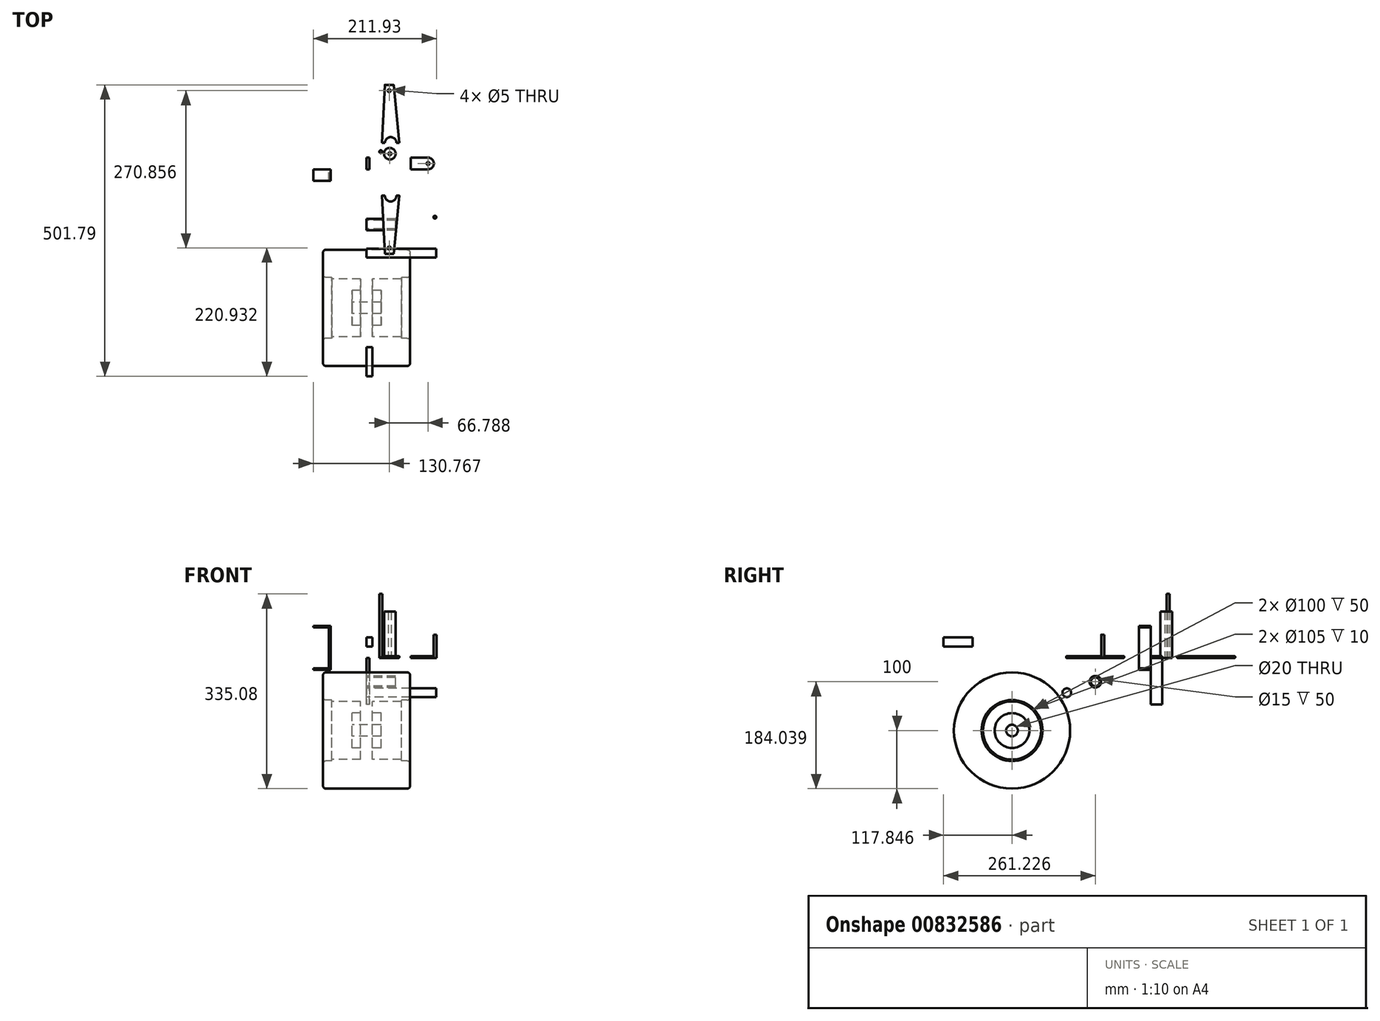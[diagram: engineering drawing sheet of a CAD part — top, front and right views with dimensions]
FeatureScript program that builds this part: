
annotation { "Feature Type Name" : "Feature", "Feature Type Description" : "" }
export const myFeature = defineFeature(function(context is Context, id is Id, definition is map)
    precondition{}
    {
        {
            var Q0;
            Q0=qCreatedBy(makeId("Top.planeOp"),FACE);
            var sketch = newSketch(context, id + "F0", { "sketchPlane" : qUnion([Q0])});
            skLineSegment(sketch, "E0", {"start": v(75.84, 20) * mm, "end": v(75.84, 0) * mm});
            skLineSegment(sketch, "E1", {"start": v(75.84, 0) * mm, "end": v(105.84, 0) * mm});
            skLineSegment(sketch, "E2", {"start": v(105.84, 20) * mm, "end": v(75.84, 20) * mm});
            skArc(sketch, "E3", {"start": v(105.84, 0) * mm, "mid": v(115.84, 10) * mm, "end": v(105.84, 20) * mm});
            skCircle(sketch, "E4", {"center": v(105.84, 10) * mm, "radius": 2.5 * mm});
            skSolve(sketch);
        }
        {
            var Q0;
            Q0=qCreatedBy(makeId("Right.planeOp"),FACE);
            var sketch = newSketch(context, id + "F1", { "sketchPlane" : qUnion([Q0])});
            skLineSegment(sketch, "E5", {"start": v(0, 0) * mm, "end": v(0, -80) * mm});
            skLineSegment(sketch, "E6", {"start": v(0, -80) * mm, "end": v(20, -80) * mm});
            skLineSegment(sketch, "E7", {"start": v(20, -80) * mm, "end": v(20, 0) * mm});
            skLineSegment(sketch, "E8", {"start": v(20, 0) * mm, "end": v(0, 0) * mm});
            skSolve(sketch);
        }
        {
            var Q0;
            Q0 = qSketchRegion(id + "F1", true);
            extrude(context, id + "F2", {"entities" : qUnion([Q0]), "depth" : 5 * mm, "offsetDistance" : 25.4 * mm});
        }
        {
            var Q0;
            Q0=qCreatedBy(makeId("Top.planeOp"),FACE);
            var sketch = newSketch(context, id + "F3", { "sketchPlane" : qUnion([Q0])});
            skCircle(sketch, "E9", {"center": v(24.54, 30.27) * mm, "radius": 2.5 * mm});
            skSolve(sketch);
        }
        {
            var Q0;
            Q0=qCreatedBy(makeId("Top.planeOp"),FACE);
            var sketch = newSketch(context, id + "F4", { "sketchPlane" : qUnion([Q0])});
            skCircle(sketch, "E10", {"center": v(40.1, 26.85) * mm, "radius": 10 * mm});
            skCircle(sketch, "E11", {"center": v(40.1, 26.85) * mm, "radius": 2.5 * mm});
            skSolve(sketch);
        }
        {
            var Q0;
            Q0=makeQuery(id+"F3.imprint","IMPRINT",FACE,{"disambiguationData":[TD([[makeQuery(id+"F3.imprint","IMPRINT",EDGE,{"derivedFrom":sQuery(id+"F3.wireOp",EDGE,"E9")}),1.0]])]});
            extrude(context, id + "F5", {"entities" : qUnion([Q0]), "depth" : 110 * mm, "offsetDistance" : 25.4 * mm});
        }
        {
            var Q0;
            Q0=makeQuery(id+"F4.imprint","IMPRINT",FACE,{"disambiguationData":[TD([[makeQuery(id+"F4.imprint","IMPRINT",EDGE,{"derivedFrom":sQuery(id+"F4.wireOp",EDGE,"E10")}),1.0]])]});
            extrude(context, id + "F6", {"entities" : qUnion([Q0]), "depth" : 80 * mm, "offsetDistance" : 25.4 * mm});
        }
        {
            var Q0;
            Q0=qCreatedBy(makeId("Top.planeOp"),FACE);
            var sketch = newSketch(context, id + "F7", { "sketchPlane" : qUnion([Q0])});
            skArc(sketch, "E12", {"start": v(31.55, -45.43) * mm, "mid": v(41.55, -55.43) * mm, "end": v(51.55, -45.43) * mm});
            skLineSegment(sketch, "E13", {"start": v(31.55, -145.43) * mm, "end": v(26.55, -45.43) * mm});
            skLineSegment(sketch, "E14", {"start": v(51.55, -45.43) * mm, "end": v(56.55, -45.43) * mm});
            skLineSegment(sketch, "E15", {"start": v(56.55, -45.43) * mm, "end": v(46.55, -145.43) * mm});
            skLineSegment(sketch, "E16", {"start": v(26.55, -45.43) * mm, "end": v(31.55, -45.43) * mm});
            skLineSegment(sketch, "E17", {"start": v(31.55, -145.43) * mm, "end": v(46.55, -145.43) * mm});
            skCircle(sketch, "E18", {"center": v(39.05, -135.43) * mm, "radius": 2.5 * mm});
            skSolve(sketch);
        }
        {
            var Q0;
            Q0=makeQuery(id+"F7.imprint","IMPRINT",FACE,{"disambiguationData":[TD([[makeQuery(id+"F7.imprint","IMPRINT",EDGE,{"derivedFrom":sQuery(id+"F7.wireOp",EDGE,"E12")}),-1.0]])]});
            extrude(context, id + "F8", {"entities" : qUnion([Q0]), "depth" : 3 * mm, "offsetDistance" : 25.4 * mm});
        }
        {
            var Q0;
            Q0=qCreatedBy(makeId("Top.planeOp"),FACE);
            var sketch = newSketch(context, id + "F9", { "sketchPlane" : qUnion([Q0])});
            skCircle(sketch, "E19", {"center": v(117.71, -82.43) * mm, "radius": 2.5 * mm});
            skSolve(sketch);
        }
        {
            var Q0;
            Q0=makeQuery(id+"F9.imprint","IMPRINT",FACE,{"disambiguationData":[TD([[makeQuery(id+"F9.imprint","IMPRINT",EDGE,{"derivedFrom":sQuery(id+"F9.wireOp",EDGE,"E19")}),1.0]])]});
            extrude(context, id + "F10", {"entities" : qUnion([Q0]), "depth" : 40 * mm, "offsetDistance" : 25.4 * mm});
        }
        {
            var Q0;
            Q0=makeQuery(id+"F0.imprint","IMPRINT",FACE,{"disambiguationData":[TD([[makeQuery(id+"F0.imprint","IMPRINT",EDGE,{"derivedFrom":sQuery(id+"F0.wireOp",EDGE,"E0")}),1.0]])]});
            extrude(context, id + "F11", {"entities" : qUnion([Q0]), "depth" : 3 * mm, "offsetDistance" : 25 * mm});
        }
        {
            var Q0;
            Q0=qCreatedBy(makeId("Front.planeOp"),FACE);
            var sketch = newSketch(context, id + "F12", { "sketchPlane" : qUnion([Q0])});
            skLineSegment(sketch, "E20.bottom", {"start": v(-91.72, -20.78) * mm, "end": v(-61.72, -20.78) * mm});
            skLineSegment(sketch, "E20.top", {"start": v(-91.72, -17.78) * mm, "end": v(-61.72, -17.78) * mm});
            skLineSegment(sketch, "E20.left", {"start": v(-91.72, -20.78) * mm, "end": v(-91.72, -17.78) * mm});
            skLineSegment(sketch, "E20.right", {"start": v(-61.72, -20.78) * mm, "end": v(-61.72, -17.78) * mm});
            skLineSegment(sketch, "E21.bottom", {"start": v(-61.72, 52.22) * mm, "end": v(-91.72, 52.22) * mm});
            skLineSegment(sketch, "E21.top", {"start": v(-61.72, 55.22) * mm, "end": v(-91.72, 55.22) * mm});
            skLineSegment(sketch, "E21.left", {"start": v(-61.72, 52.22) * mm, "end": v(-61.72, 55.22) * mm});
            skLineSegment(sketch, "E21.right", {"start": v(-91.72, 52.22) * mm, "end": v(-91.72, 55.22) * mm});
            skLineSegment(sketch, "E22.bottom", {"start": v(-61.72, 52.22) * mm, "end": v(-64.72, 52.22) * mm});
            skLineSegment(sketch, "E22.top", {"start": v(-61.72, -17.78) * mm, "end": v(-64.72, -17.78) * mm});
            skLineSegment(sketch, "E22.left", {"start": v(-61.72, 52.22) * mm, "end": v(-61.72, -17.78) * mm});
            skLineSegment(sketch, "E22.right", {"start": v(-64.72, 52.22) * mm, "end": v(-64.72, -17.78) * mm});
            skSolve(sketch);
        }
        {
            var Q0;
            Q0=makeQuery(id+"F12.imprint","IMPRINT",FACE,{"disambiguationData":[TD([[makeQuery(id+"F12.imprint","IMPRINT",EDGE,{"derivedFrom":sQuery(id+"F12.wireOp",EDGE,"E21.top")}),1.0]])]});
            var Q1;
            Q1=makeQuery(id+"F12.imprint","IMPRINT",FACE,{"disambiguationData":[TD([[makeQuery(id+"F12.imprint","IMPRINT",EDGE,{"derivedFrom":sQuery(id+"F12.wireOp",EDGE,"E20.bottom")}),1.0]])]});
            extrude(context, id + "F13", {"entities" : qUnion([Q0, Q1]), "depth" : 20 * mm, "offsetDistance" : 25 * mm});
        }
        {
            var Q0;
            {var subQ0=sQuery(id+"F12.wireOp",EDGE,"E22.left");Q0=makeQuery(id+"F12.imprint","IMPRINT",FACE,{"disambiguationData":[TD([[makeQuery(id+"F12.imprint","IMPRINT",EDGE,{"derivedFrom":subQ0}),-1.0]])]});}
            extrude(context, id + "F14", {"entities" : qUnion([Q0]), "depth" : 20 * mm, "offsetDistance" : 25 * mm});
        }
        {
            var Q0;
            Q0=qCreatedBy(makeId("Right.planeOp"),FACE);
            var sketch = newSketch(context, id + "F15", { "sketchPlane" : qUnion([Q0])});
            skCircle(sketch, "E23", {"center": v(-95.13, -41.04) * mm, "radius": 10 * mm});
            skCircle(sketch, "E24", {"center": v(-95.13, -41.04) * mm, "radius": 7.5 * mm});
            skSolve(sketch);
        }
        {
            var Q0;
            Q0=makeQuery(id+"F15.imprint","IMPRINT",FACE,{"disambiguationData":[TD([[makeQuery(id+"F15.imprint","IMPRINT",EDGE,{"derivedFrom":sQuery(id+"F15.wireOp",EDGE,"E23")}),1.0]])]});
            extrude(context, id + "F16", {"entities" : qUnion([Q0]), "depth" : 50 * mm, "offsetDistance" : 25 * mm});
        }
        {
            var Q0;
            Q0=qCreatedBy(makeId("Right.planeOp"),FACE);
            var sketch = newSketch(context, id + "F17", { "sketchPlane" : qUnion([Q0])});
            skCircle(sketch, "E25", {"center": v(-144.24, -59.98) * mm, "radius": 7.5 * mm});
            skSolve(sketch);
        }
        {
            var Q0;
            Q0=qCreatedBy(makeId("Right.planeOp"),FACE);
            var sketch = newSketch(context, id + "F18", { "sketchPlane" : qUnion([Q0])});
            skCircle(sketch, "E26", {"center": v(-238.51, -125.08) * mm, "radius": 100 * mm});
            skCircle(sketch, "E27", {"center": v(-238.51, -125.08) * mm, "radius": 10 * mm});
            skCircle(sketch, "E28", {"center": v(-238.51, -125.08) * mm, "radius": 50 * mm});
            skCircle(sketch, "E29", {"center": v(-238.51, -125.08) * mm, "radius": 30 * mm});
            skCircle(sketch, "E30", {"center": v(-238.51, -125.08) * mm, "radius": 52.5 * mm});
            skSolve(sketch);
        }
        {
            var Q0;
            Q0=makeQuery(id+"F17.imprint","IMPRINT",FACE,{"disambiguationData":[TD([[makeQuery(id+"F17.imprint","IMPRINT",EDGE,{"derivedFrom":sQuery(id+"F17.wireOp",EDGE,"E25")}),1.0]])]});
            extrude(context, id + "F19", {"entities" : qUnion([Q0]), "depth" : 120 * mm, "offsetDistance" : 25 * mm});
        }
        {
            var Q0;
            Q0=makeQuery(id+"F18.imprint","IMPRINT",FACE,{"disambiguationData":[TD([[makeQuery(id+"F18.imprint","IMPRINT",EDGE,{"derivedFrom":sQuery(id+"F18.wireOp",EDGE,"E27")}),-1.0]])]});
            extrude(context, id + "F20", {"entities" : qUnion([Q0]), "endBound" : BoundingType.SYMMETRIC, "depth" : 50 * mm, "offsetDistance" : 25 * mm});
        }
        {
            var Q0;
            Q0=makeQuery(id+"F18.imprint","IMPRINT",FACE,{"disambiguationData":[TD([[makeQuery(id+"F18.imprint","IMPRINT",EDGE,{"derivedFrom":sQuery(id+"F18.wireOp",EDGE,"E28")}),1.0]])]});
            extrude(context, id + "F21", {"entities" : qUnion([Q0]), "operationType" : NewBodyOperationType.ADD, "endBound" : BoundingType.SYMMETRIC, "depth" : 20 * mm, "offsetDistance" : 25 * mm});
        }
        {
            var Q0;
            Q0=makeQuery(id+"F18.imprint","IMPRINT",FACE,{"disambiguationData":[TD([[makeQuery(id+"F18.imprint","IMPRINT",EDGE,{"derivedFrom":sQuery(id+"F18.wireOp",EDGE,"E28")}),-1.0]])]});
            extrude(context, id + "F22", {"entities" : qUnion([Q0]), "operationType" : NewBodyOperationType.ADD, "endBound" : BoundingType.SYMMETRIC, "depth" : 120 * mm, "offsetDistance" : 25 * mm});
        }
        {
            var Q0;
            Q0=makeQuery(id+"F18.imprint","IMPRINT",FACE,{"disambiguationData":[TD([[makeQuery(id+"F18.imprint","IMPRINT",EDGE,{"derivedFrom":sQuery(id+"F18.wireOp",EDGE,"E26")}),1.0]])]});
            extrude(context, id + "F23", {"entities" : qUnion([Q0]), "operationType" : NewBodyOperationType.ADD, "endBound" : BoundingType.SYMMETRIC, "depth" : 150 * mm, "offsetDistance" : 25 * mm});
        }
        {
            var Q0;
            Q0=makeQuery(id+"F23.opExtrude","CAP_FACE",FACE,{"disambiguationData":[OSD([sQuery(id+"F18.wireOp",EDGE,"E26"),sQuery(id+"F18.wireOp",EDGE,"E30")])],"isStart":false});
            var Q1;
            Q1=makeQuery(id+"F23.opExtrude","SWEPT_FACE",FACE,{"disambiguationData":[OSD([sQuery(id+"F18.wireOp",EDGE,"E26")])]});
            var Q2;
            Q2=makeQuery(id+"F23.opExtrude","CAP_FACE",FACE,{"disambiguationData":[OSD([sQuery(id+"F18.wireOp",EDGE,"E26"),sQuery(id+"F18.wireOp",EDGE,"E30")])],"isStart":true});
            fillet(context, id + "F24", {"entities" : qUnion([Q0, Q1, Q2]), "radius" : 5 * mm, "tangentPropagation" : true, "allowEdgeOverflow" : false});
        }
        {
            var Q0;
            Q0=makeQuery(id+"F11.opExtrude","CAP_EDGE",EDGE,{"disambiguationData":[OSD([sQuery(id+"F0.wireOp",EDGE,"E4")])],"isStart":false});
            var Q1;
            Q1=makeQuery(id+"F11.opExtrude","CAP_EDGE",EDGE,{"disambiguationData":[OSD([sQuery(id+"F0.wireOp",EDGE,"E4")])],"isStart":true});
            fillet(context, id + "F25", {"entities" : qUnion([Q0, Q1]), "radius" : 1 * mm, "tangentPropagation" : true, "allowEdgeOverflow" : false});
        }
        {
            var Q0;
            Q0=makeQuery(id+"F8.opExtrude","CAP_FACE",FACE,{"disambiguationData":[OSD([sQuery(id+"F7.wireOp",EDGE,"E12"),sQuery(id+"F7.wireOp",EDGE,"E13"),sQuery(id+"F7.wireOp",EDGE,"E14"),sQuery(id+"F7.wireOp",EDGE,"E15"),sQuery(id+"F7.wireOp",EDGE,"E16"),sQuery(id+"F7.wireOp",EDGE,"E17"),sQuery(id+"F7.wireOp",EDGE,"E18")])],"isStart":false});
            var Q1;
            Q1=makeQuery(id+"F8.opExtrude","CAP_FACE",FACE,{"disambiguationData":[OSD([sQuery(id+"F7.wireOp",EDGE,"E12"),sQuery(id+"F7.wireOp",EDGE,"E13"),sQuery(id+"F7.wireOp",EDGE,"E14"),sQuery(id+"F7.wireOp",EDGE,"E15"),sQuery(id+"F7.wireOp",EDGE,"E16"),sQuery(id+"F7.wireOp",EDGE,"E17"),sQuery(id+"F7.wireOp",EDGE,"E18")])],"isStart":true});
            var Q2;
            Q2=makeQuery(id+"F8.opExtrude","CAP_EDGE",EDGE,{"disambiguationData":[OSD([sQuery(id+"F7.wireOp",EDGE,"E18")])],"isStart":true});
            var Q3;
            Q3=makeQuery(id+"F8.opExtrude","CAP_EDGE",EDGE,{"disambiguationData":[OSD([sQuery(id+"F7.wireOp",EDGE,"E18")])],"isStart":false});
            fillet(context, id + "F26", {"entities" : qUnion([Q0, Q1, Q2, Q3]), "radius" : 1 * mm, "tangentPropagation" : true, "allowEdgeOverflow" : false});
        }
        {
            var Q0;
            Q0=qCreatedBy(makeId("Right.planeOp"),FACE);
            var sketch = newSketch(context, id + "F27", { "sketchPlane" : qUnion([Q0])});
            skLineSegment(sketch, "E31.bottom", {"start": v(-356.36, 35.55) * mm, "end": v(-306.36, 35.55) * mm});
            skLineSegment(sketch, "E31.top", {"start": v(-356.36, 19.55) * mm, "end": v(-306.36, 19.55) * mm});
            skLineSegment(sketch, "E31.left", {"start": v(-356.36, 35.55) * mm, "end": v(-356.36, 19.55) * mm});
            skLineSegment(sketch, "E31.right", {"start": v(-306.36, 35.55) * mm, "end": v(-306.36, 19.55) * mm});
            skSolve(sketch);
        }
        {
            var Q0;
            Q0=makeQuery(id+"F27.imprint","IMPRINT",FACE,{"disambiguationData":[TD([[makeQuery(id+"F27.imprint","IMPRINT",EDGE,{"derivedFrom":sQuery(id+"F27.wireOp",EDGE,"E31.bottom")}),-1.0]])]});
            extrude(context, id + "F28", {"entities" : qUnion([Q0]), "depth" : 10 * mm, "offsetDistance" : 25 * mm});
        }
        {
            var Q0;
            Q0=makeQuery(id+"F8.opExtrude","SWEPT_BODY",BODY,{"disambiguationData":[OSD([sQuery(id+"F7.wireOp",EDGE,"E12"),sQuery(id+"F7.wireOp",EDGE,"E13"),sQuery(id+"F7.wireOp",EDGE,"E14"),sQuery(id+"F7.wireOp",EDGE,"E15"),sQuery(id+"F7.wireOp",EDGE,"E16"),sQuery(id+"F7.wireOp",EDGE,"E17"),sQuery(id+"F7.wireOp",EDGE,"E18")])]});
            var Q1;
            Q1=qCreatedBy(makeId("Front.planeOp"),FACE);
            mirror(context, id + "F29", {"entities" : qUnion([Q0]), "mirrorPlane" : qUnion([Q1])});
        }
    });
